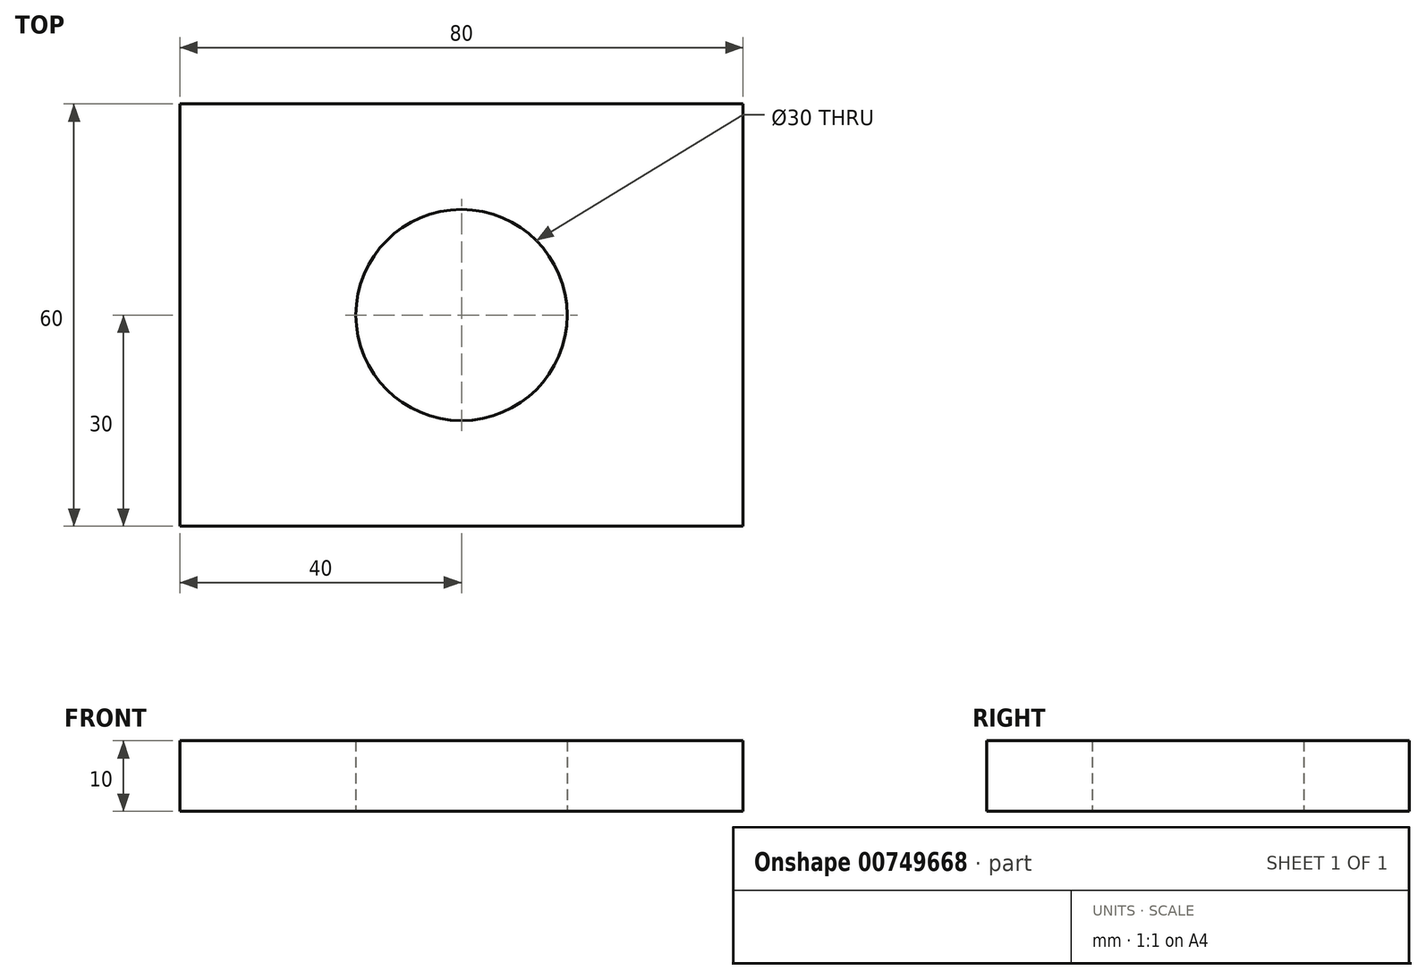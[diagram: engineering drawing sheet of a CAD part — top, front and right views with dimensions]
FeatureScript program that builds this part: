
annotation { "Feature Type Name" : "Feature", "Feature Type Description" : "" }
export const myFeature = defineFeature(function(context is Context, id is Id, definition is map)
    precondition{}
    {
        {
            var Q0;
            Q0=qCreatedBy(makeId("Top.planeOp"),FACE);
            var sketch = newSketch(context, id + "F0", { "sketchPlane" : qUnion([Q0])});
            skLineSegment(sketch, "E0.bottom", {"start": v(0, 0) * mm, "end": v(80, 0) * mm});
            skLineSegment(sketch, "E0.top", {"start": v(0, 60) * mm, "end": v(80, 60) * mm});
            skLineSegment(sketch, "E0.left", {"start": v(0, 0) * mm, "end": v(0, 60) * mm});
            skLineSegment(sketch, "E0.right", {"start": v(80, 0) * mm, "end": v(80, 60) * mm});
            skLineSegment(sketch, "E1", {"start": v(80, 60) * mm, "end": v(40, 60) * mm, "construction": true});
            skLineSegment(sketch, "E2", {"start": v(40, 60) * mm, "end": v(40, 30) * mm, "construction": true});
            skPoint(sketch, "E2.endSnap0", {"position": v(80, 30) * mm});
            skCircle(sketch, "E3", {"center": v(40, 30) * mm, "radius": 15 * mm});
            skSolve(sketch);
        }
        {
            var Q0;
            Q0=makeQuery(id+"F0.imprint","IMPRINT",FACE,{"disambiguationData":[TD([[makeQuery(id+"F0.imprint","IMPRINT",EDGE,{"derivedFrom":sQuery(id+"F0.wireOp",EDGE,"E0.bottom")}),1.0]])]});
            extrude(context, id + "F1", {"entities" : qUnion([Q0]), "depth" : 10 * mm, "offsetDistance" : 25 * mm});
        }
    });
